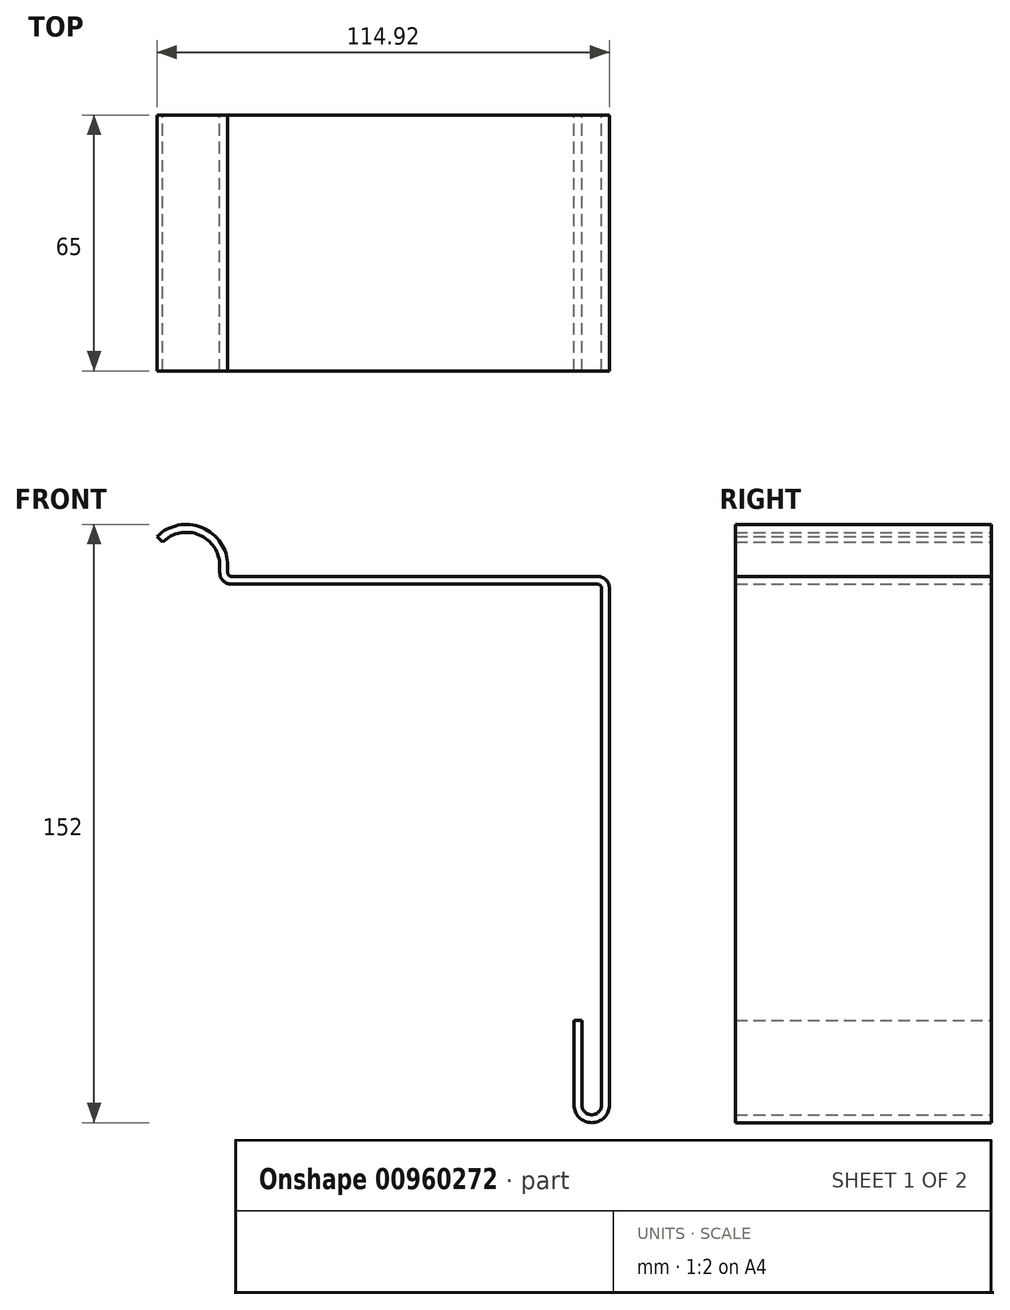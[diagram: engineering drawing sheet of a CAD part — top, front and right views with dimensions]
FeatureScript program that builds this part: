
annotation { "Feature Type Name" : "Feature", "Feature Type Description" : "" }
export const myFeature = defineFeature(function(context is Context, id is Id, definition is map)
    precondition{}
    {
        {
            var Q0;
            Q0=qCreatedBy(makeId("Front.planeOp"),FACE);
            var sketch = newSketch(context, id + "F0", { "sketchPlane" : qUnion([Q0])});
            skLineSegment(sketch, "E0.bottom", {"start": v(-50, 1.6) * mm, "end": v(50, 1.6) * mm});
            skLineSegment(sketch, "E0.top", {"start": v(-50, -1.6) * mm, "end": v(50, -1.6) * mm});
            skLineSegment(sketch, "E0.left", {"start": v(-50, 1.6) * mm, "end": v(-50, -1.6) * mm});
            skLineSegment(sketch, "E0.right", {"start": v(50, 1.6) * mm, "end": v(50, -1.6) * mm});
            skPoint(sketch, "E0.middle", {"position": v(0, 0) * mm});
            skPoint(sketch, "E1", {"position": v(-50, 6.6) * mm});
            skCircle(sketch, "E2", {"center": v(-50, 6.6) * mm, "radius": 5 * mm});
            skCircle(sketch, "E3", {"center": v(-50, 6.6) * mm, "radius": 8.2 * mm});
            skLineSegment(sketch, "E4.bottom", {"start": v(-50, 6.6) * mm, "end": v(-41.8, 6.6) * mm});
            skLineSegment(sketch, "E4.top", {"start": v(-50, 1.6) * mm, "end": v(-41.8, 1.6) * mm});
            skLineSegment(sketch, "E4.left", {"start": v(-50, 6.6) * mm, "end": v(-50, 1.6) * mm});
            skLineSegment(sketch, "E4.right", {"start": v(-41.8, 6.6) * mm, "end": v(-41.8, 1.6) * mm});
            skLineSegment(sketch, "E5.bottom", {"start": v(-50, 1.6) * mm, "end": v(-45, 1.6) * mm});
            skLineSegment(sketch, "E5.top", {"start": v(-50, 6.6) * mm, "end": v(-45, 6.6) * mm});
            skLineSegment(sketch, "E5.left", {"start": v(-50, 1.6) * mm, "end": v(-50, 6.6) * mm});
            skLineSegment(sketch, "E5.right", {"start": v(-45, 1.6) * mm, "end": v(-45, 6.6) * mm});
            skLineSegment(sketch, "E6.bottom", {"start": v(-45, 1.6) * mm, "end": v(-41.8, 1.6) * mm});
            skLineSegment(sketch, "E6.top", {"start": v(-45, 2.1) * mm, "end": v(-41.8, 2.1) * mm});
            skLineSegment(sketch, "E6.left", {"start": v(-45, 1.6) * mm, "end": v(-45, 2.1) * mm});
            skLineSegment(sketch, "E6.right", {"start": v(-41.8, 1.6) * mm, "end": v(-41.8, 2.1) * mm});
            skLineSegment(sketch, "E7.bottom", {"start": v(50, 1.6) * mm, "end": v(53.2, 1.6) * mm});
            skLineSegment(sketch, "E7.top", {"start": v(50, -131.6) * mm, "end": v(53.2, -131.6) * mm});
            skLineSegment(sketch, "E7.left", {"start": v(50, 1.6) * mm, "end": v(50, -131.6) * mm});
            skLineSegment(sketch, "E7.right", {"start": v(53.2, 1.6) * mm, "end": v(53.2, -131.6) * mm});
            skSolve(sketch);
        }
        {
            var Q0;
            {var subQ0=sQuery(id+"F0.wireOp",EDGE,"E0.left");Q0=makeQuery(id+"F0.imprint","IMPRINT",FACE,{"disambiguationData":[TD([[makeQuery(id+"F0.imprint","IMPRINT",EDGE,{"derivedFrom":subQ0}),-1.0]])]});}
            var Q1;
            {var subQ3=sQuery(id+"F0.wireOp",EDGE,"E6.top");var subQ5=sQuery(id+"F0.wireOp",EDGE,"E5.right");var subQ7=makeQuery(id+"F0.imprint","INTERSECT",VERTEX,{"derivedFrom":[subQ5,subQ3]});Q1=makeQuery(id+"F0.imprint","IMPRINT",FACE,{"disambiguationData":[TD([[makeQuery(id+"F0.imprint","IMPRINT",EDGE,{"disambiguationData":[TD([[subQ7,-1.0]])],"derivedFrom":subQ3}),1.0]])]});}
            var Q2;
            {var subQ1=sQuery(id+"F0.wireOp",EDGE,"E0.top");Q2=makeQuery(id+"F0.imprint","IMPRINT",FACE,{"disambiguationData":[TD([[makeQuery(id+"F0.imprint","IMPRINT",EDGE,{"derivedFrom":subQ1}),1.0]])]});}
            var Q3;
            {var subQ0=sQuery(id+"F0.wireOp",EDGE,"E0.left");Q3=makeQuery(id+"F0.imprint","IMPRINT",FACE,{"disambiguationData":[TD([[makeQuery(id+"F0.imprint","IMPRINT",EDGE,{"derivedFrom":subQ0}),1.0]])]});}
            var Q4;
            {var subQ0=sQuery(id+"F0.wireOp",EDGE,"E4.right");var subQ3=sQuery(id+"F0.wireOp",EDGE,"E6.top");var subQ5=makeQuery(id+"F0.imprint","INTERSECT",VERTEX,{"derivedFrom":[subQ0,subQ3]});Q4=makeQuery(id+"F0.imprint","IMPRINT",FACE,{"disambiguationData":[TD([[makeQuery(id+"F0.imprint","IMPRINT",EDGE,{"disambiguationData":[TD([[subQ5,1.0]])],"derivedFrom":subQ3}),1.0]])]});}
            var Q5;
            Q5=makeQuery(id+"F0.imprint","IMPRINT",FACE,{"disambiguationData":[TD([[makeQuery(id+"F0.imprint","IMPRINT",EDGE,{"derivedFrom":sQuery(id+"F0.wireOp",EDGE,"E0.right")}),1.0]])]});
            extrude(context, id + "F1", {"entities" : qUnion([Q0, Q1, Q2, Q3, Q4, Q5]), "depth" : 19 * mm, "offsetDistance" : 25 * mm});
        }
        {
            var Q0;
            Q0=makeQuery(id+"F1.opExtrude","SWEPT_EDGE",EDGE,{"disambiguationData":[OSD([sQuery(id+"F0.wireOp",EDGE,"E0.top"),sQuery(id+"F0.wireOp",EDGE,"E0.right"),sQuery(id+"F0.wireOp",EDGE,"E7.left")])]});
            fillet(context, id + "F2", {"entities" : qUnion([Q0]), "radius" : 2 * mm, "tangentPropagation" : true, "allowEdgeOverflow" : false});
        }
        {
            var Q0;
            Q0=makeQuery(id+"F1.opExtrude","CAP_FACE",FACE,{"disambiguationData":[OSD([sQuery(id+"F0.wireOp",EDGE,"E0.bottom"),sQuery(id+"F0.wireOp",EDGE,"E0.top"),sQuery(id+"F0.wireOp",EDGE,"E2"),sQuery(id+"F0.wireOp",EDGE,"E3"),sQuery(id+"F0.wireOp",EDGE,"E4.right"),sQuery(id+"F0.wireOp",EDGE,"E5.right"),sQuery(id+"F0.wireOp",EDGE,"E6.top"),sQuery(id+"F0.wireOp",EDGE,"E7.bottom"),sQuery(id+"F0.wireOp",EDGE,"E7.top"),sQuery(id+"F0.wireOp",EDGE,"E7.left"),sQuery(id+"F0.wireOp",EDGE,"E7.right")])],"isStart":false});
            extrude(context, id + "F3", {"entities" : qUnion([Q0]), "operationType" : NewBodyOperationType.REMOVE, "oppositeDirection" : true, "depth" : 18 * mm, "offsetDistance" : 25 * mm});
        }
        {
            var Q0;
            Q0=makeQuery(id+"F3.boolean.opBoolean","COPY",FACE,{"derivedFrom":makeQuery(id+"F3.opExtrude","CAP_FACE",FACE,{"disambiguationData":[OSD([sQuery(id+"F0.wireOp",EDGE,"E0.bottom"),sQuery(id+"F0.wireOp",EDGE,"E0.top"),sQuery(id+"F0.wireOp",EDGE,"E2"),sQuery(id+"F0.wireOp",EDGE,"E3"),sQuery(id+"F0.wireOp",EDGE,"E4.right"),sQuery(id+"F0.wireOp",EDGE,"E5.right"),sQuery(id+"F0.wireOp",EDGE,"E6.top"),sQuery(id+"F0.wireOp",EDGE,"E7.bottom"),sQuery(id+"F0.wireOp",EDGE,"E7.top"),sQuery(id+"F0.wireOp",EDGE,"E7.left"),sQuery(id+"F0.wireOp",EDGE,"E7.right")])],"isStart":false})});
            extrude(context, id + "F4", {"entities" : qUnion([Q0]), "operationType" : NewBodyOperationType.REMOVE, "oppositeDirection" : true, "depth" : 1 * mm, "offsetDistance" : 25 * mm});
        }
        {
            var Q0;
            Q0=qCreatedBy(makeId("Front.planeOp"),FACE);
            var sketch = newSketch(context, id + "F5", { "sketchPlane" : qUnion([Q0])});
            skLineSegment(sketch, "E8.bottom", {"start": v(-10.63, 7.7) * mm, "end": v(-10.63, 7.7) * mm});
            skLineSegment(sketch, "E9.right", {"start": v(-5.13, 6) * mm, "end": v(-5.13, 7.7) * mm});
            skLineSegment(sketch, "E10.trimOffspring", {"start": v(-7.43, 7.7) * mm, "end": v(-7.43, 7.7) * mm});
            skLineSegment(sketch, "E11", {"start": v(-4.13, 5) * mm, "end": v(88.87, 5) * mm});
            skLineSegment(sketch, "E12", {"start": v(-7.13, 7.7) * mm, "end": v(-7.13, 6) * mm});
            skLineSegment(sketch, "E13", {"start": v(-4.13, 3) * mm, "end": v(88.87, 3) * mm});
            skLineSegment(sketch, "E14", {"start": v(-21.64, 13.72) * mm, "end": v(-23.05, 15.13) * mm});
            skPoint(sketch, "E15", {"position": v(-4.13, 6) * mm});
            skArc(sketch, "E16", {"start": v(-5.13, 6) * mm, "mid": v(-4.84, 5.3) * mm, "end": v(-4.13, 5) * mm});
            skArc(sketch, "E17", {"start": v(-7.13, 6) * mm, "mid": v(-6.25, 3.88) * mm, "end": v(-4.13, 3) * mm});
            skPoint(sketch, "E18.orphan", {"position": v(-5.13, 5) * mm});
            skPoint(sketch, "E19", {"position": v(-15.63, 7.7) * mm});
            skArc(sketch, "E20", {"start": v(-7.13, 7.7) * mm, "mid": v(-12.38, 15.56) * mm, "end": v(-21.64, 13.72) * mm});
            skArc(sketch, "E21", {"start": v(-5.13, 7.7) * mm, "mid": v(-11.61, 17.4) * mm, "end": v(-23.05, 15.13) * mm});
            skPoint(sketch, "E22", {"position": v(88.87, 2) * mm});
            skArc(sketch, "E23", {"start": v(89.87, 2) * mm, "mid": v(89.58, 2.71) * mm, "end": v(88.87, 3) * mm});
            skArc(sketch, "E24.trimOffspring", {"start": v(91.87, 2) * mm, "mid": v(91, 4.13) * mm, "end": v(88.87, 5) * mm});
            skLineSegment(sketch, "E25", {"start": v(82.87, -107.8) * mm, "end": v(84.87, -107.8) * mm});
            skPoint(sketch, "E26", {"position": v(87.37, -129.3) * mm});
            skArc(sketch, "E27", {"start": v(84.87, -129.3) * mm, "mid": v(87.37, -131.8) * mm, "end": v(89.87, -129.3) * mm});
            skArc(sketch, "E28", {"start": v(82.87, -129.3) * mm, "mid": v(87.37, -133.8) * mm, "end": v(91.87, -129.3) * mm});
            skLineSegment(sketch, "E29", {"start": v(82.87, -107.8) * mm, "end": v(82.87, -129.3) * mm});
            skLineSegment(sketch, "E30", {"start": v(84.87, -107.8) * mm, "end": v(84.87, -129.3) * mm});
            skLineSegment(sketch, "E31", {"start": v(89.87, 2) * mm, "end": v(89.87, -129.3) * mm});
            skLineSegment(sketch, "E32", {"start": v(91.87, -129.3) * mm, "end": v(91.87, 2) * mm});
            skSolve(sketch);
        }
        {
            var Q0;
            Q0=qSketchRegion(id+"F5",true);
            extrude(context, id + "F6", {"entities" : qUnion([Q0]), "depth" : 65 * mm, "offsetDistance" : 25 * mm});
        }
    });
